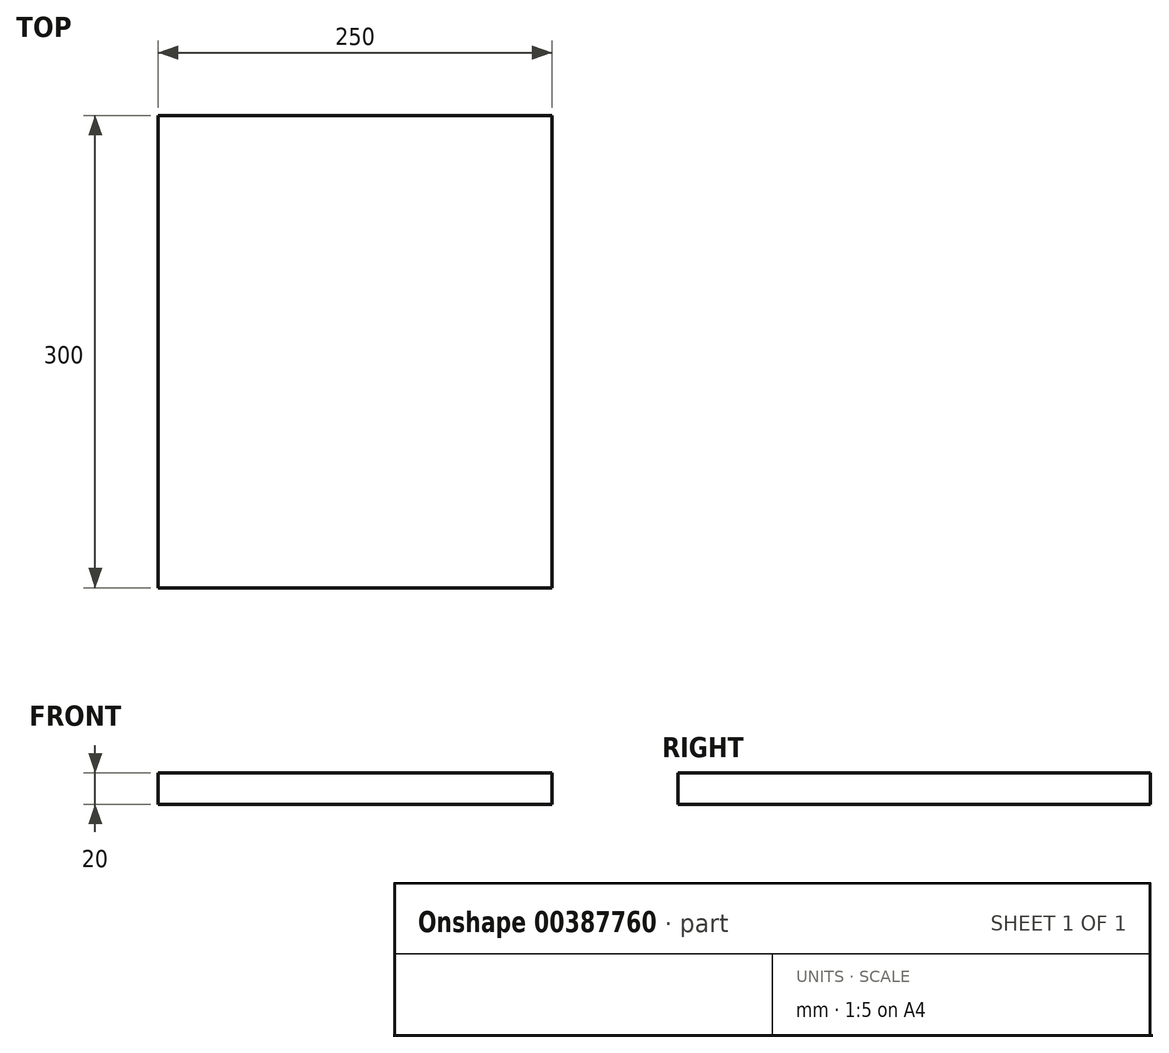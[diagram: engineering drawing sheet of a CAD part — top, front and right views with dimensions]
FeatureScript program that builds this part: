
annotation { "Feature Type Name" : "Feature", "Feature Type Description" : "" }
export const myFeature = defineFeature(function(context is Context, id is Id, definition is map)
    precondition{}
    {
        {
            var Q0;
            Q0=qCreatedBy(makeId("Top.planeOp"),FACE);
            var sketch = newSketch(context, id + "F0", { "sketchPlane" : qUnion([Q0])});
            skLineSegment(sketch, "E0.bottom", {"start": v(0, 0) * mm, "end": v(250, 0) * mm});
            skLineSegment(sketch, "E0.top", {"start": v(0, 300) * mm, "end": v(250, 300) * mm});
            skLineSegment(sketch, "E0.left", {"start": v(0, 0) * mm, "end": v(0, 300) * mm});
            skLineSegment(sketch, "E0.right", {"start": v(250, 0) * mm, "end": v(250, 300) * mm});
            skSolve(sketch);
        }
        {
            var Q0;
            Q0=makeQuery(id+"F0.imprint","IMPRINT",FACE,{"disambiguationData":[TD([[makeQuery(id+"F0.imprint","IMPRINT",EDGE,{"derivedFrom":sQuery(id+"F0.wireOp",EDGE,"E0.bottom")}),1.0]])]});
            extrude(context, id + "F1", {"entities" : qUnion([Q0]), "depth" : 20 * mm});
        }
    });
